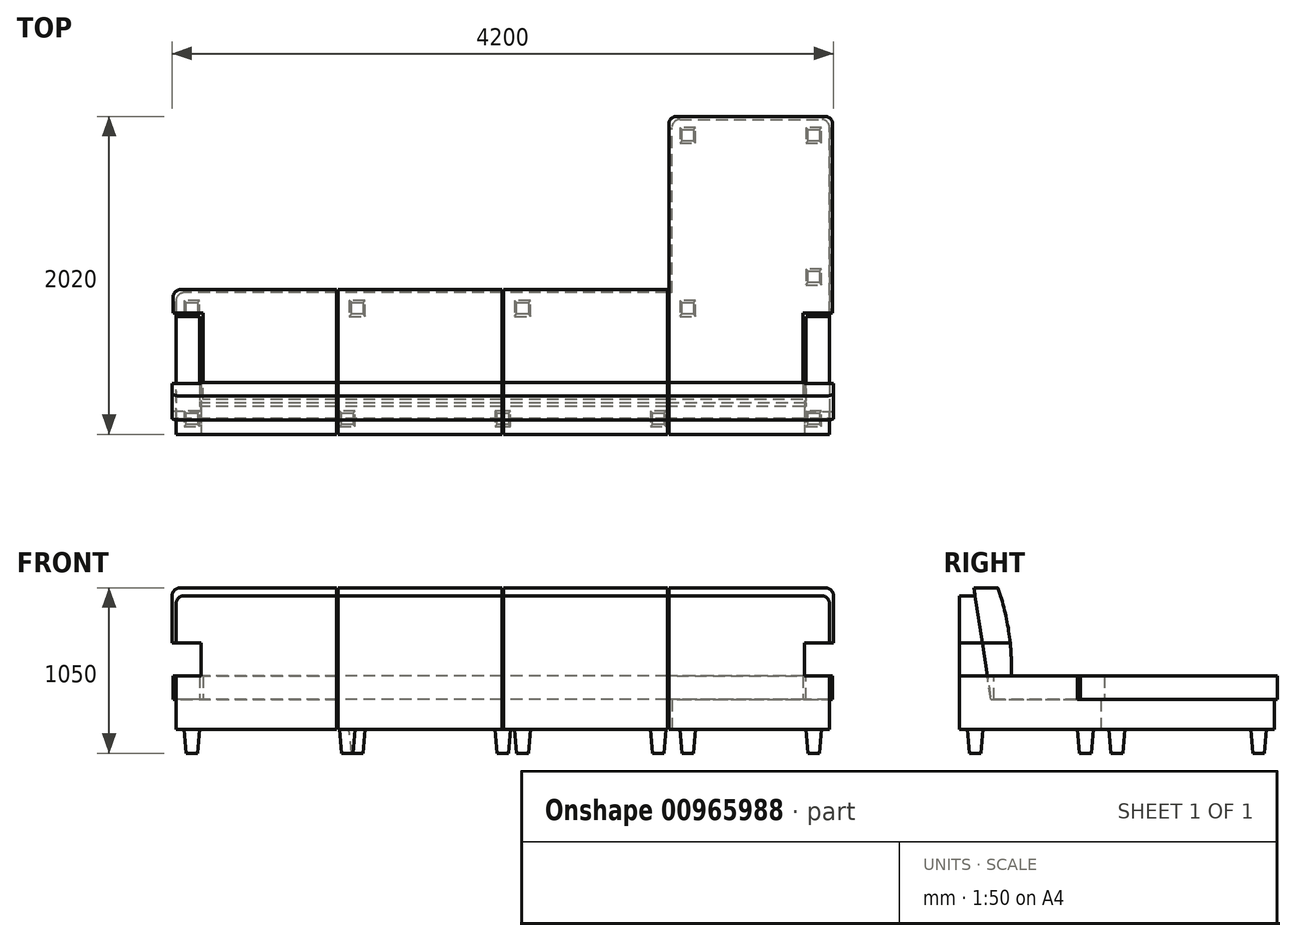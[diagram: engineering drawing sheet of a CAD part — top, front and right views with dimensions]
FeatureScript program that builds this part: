
annotation { "Feature Type Name" : "Feature", "Feature Type Description" : "" }
export const myFeature = defineFeature(function(context is Context, id is Id, definition is map)
    precondition{}
    {
        {
            var Q0;
            Q0=qCreatedBy(makeId("Right.planeOp"),FACE);
            var sketch = newSketch(context, id + "F0", { "sketchPlane" : qUnion([Q0])});
            skLineSegment(sketch, "E0", {"start": v(0, 150) * mm, "end": v(0, 1000) * mm});
            skLineSegment(sketch, "E1", {"start": v(0, 1000) * mm, "end": v(100, 1000) * mm});
            skLineSegment(sketch, "E2", {"start": v(100, 1000) * mm, "end": v(200, 340) * mm});
            skLineSegment(sketch, "E3", {"start": v(200, 340) * mm, "end": v(900, 340) * mm});
            skLineSegment(sketch, "E4", {"start": v(900, 340) * mm, "end": v(900, 150) * mm});
            skLineSegment(sketch, "E5", {"start": v(900, 150) * mm, "end": v(0, 150) * mm});
            skSolve(sketch);
        }
        {
            var Q0;
            Q0 = qSketchRegion(id + "F0", true);
            extrude(context, id + "F1", {"entities" : qUnion([Q0]), "depth" : 4150 * mm, "offsetDistance" : 25 * mm});
        }
        {
            var Q0;
            Q0=makeQuery(id+"F1.opExtrude","SWEPT_FACE",FACE,{"disambiguationData":[OSD([sQuery(id+"F0.wireOp",EDGE,"E5")])]});
            var sketch = newSketch(context, id + "F2", { "sketchPlane" : qUnion([Q0])});
            skLineSegment(sketch, "E6.bottom", {"start": v(3150, 0) * mm, "end": v(4150, 0) * mm});
            skLineSegment(sketch, "E6.top", {"start": v(3150, -2000) * mm, "end": v(4150, -2000) * mm});
            skLineSegment(sketch, "E6.left", {"start": v(3150, 0) * mm, "end": v(3150, -2000) * mm});
            skLineSegment(sketch, "E6.right", {"start": v(4150, 0) * mm, "end": v(4150, -2000) * mm});
            skSolve(sketch);
        }
        {
            var Q0;
            {var subQ0=sQuery(id+"F2.wireOp",EDGE,"E6.top");Q0=makeQuery(id+"F2.imprint","IMPRINT",FACE,{"disambiguationData":[TD([[makeQuery(id+"F2.imprint","IMPRINT",EDGE,{"derivedFrom":subQ0}),1.0]])]});}
            var Q1;
            Q1=makeQuery(id+"F1.opExtrude","SWEPT_FACE",FACE,{"disambiguationData":[OSD([sQuery(id+"F0.wireOp",EDGE,"E3")])]});
            extrude(context, id + "F3", {"entities" : qUnion([Q0]), "operationType" : NewBodyOperationType.ADD, "endBound" : BoundingType.UP_TO_SURFACE, "oppositeDirection" : true, "depth" : 25 * mm, "endBoundEntityFace" : qUnion([Q1]), "offsetDistance" : 25 * mm});
        }
        {
            var Q0;
            Q0=qCreatedBy(makeId("Front.planeOp"),FACE);
            var sketch = newSketch(context, id + "F4", { "sketchPlane" : qUnion([Q0])});
            skLineSegment(sketch, "E7.bottom", {"start": v(150, 690) * mm, "end": v(0, 690) * mm});
            skLineSegment(sketch, "E7.top", {"start": v(150, 340) * mm, "end": v(0, 340) * mm});
            skLineSegment(sketch, "E7.left", {"start": v(150, 690) * mm, "end": v(150, 340) * mm});
            skLineSegment(sketch, "E7.right", {"start": v(0, 690) * mm, "end": v(0, 340) * mm});
            skSolve(sketch);
        }
        {
            var Q0;
            Q0 = qSketchRegion(id + "F4", true);
            var Q1;
            Q1=makeQuery(id+"F1.opExtrude","SWEPT_FACE",FACE,{"disambiguationData":[OSD([sQuery(id+"F0.wireOp",EDGE,"E4")])]});
            extrude(context, id + "F5", {"entities" : qUnion([Q0]), "operationType" : NewBodyOperationType.ADD, "oppositeDirection" : true, "depth" : 750 * mm, "endBoundEntityFace" : qUnion([Q1]), "offsetDistance" : 25 * mm});
        }
        {
            var Q0;
            Q0=qCreatedBy(makeId("Front.planeOp"),FACE);
            var sketch = newSketch(context, id + "F6", { "sketchPlane" : qUnion([Q0])});
            skLineSegment(sketch, "E8.bottom", {"start": v(4150, 690) * mm, "end": v(4000, 690) * mm});
            skLineSegment(sketch, "E8.top", {"start": v(4150, 150) * mm, "end": v(4000, 150) * mm});
            skLineSegment(sketch, "E8.left", {"start": v(4150, 690) * mm, "end": v(4150, 150) * mm});
            skLineSegment(sketch, "E8.right", {"start": v(4000, 690) * mm, "end": v(4000, 150) * mm});
            skSolve(sketch);
        }
        {
            var Q0;
            Q0 = qSketchRegion(id + "F6", true);
            extrude(context, id + "F7", {"entities" : qUnion([Q0]), "operationType" : NewBodyOperationType.ADD, "oppositeDirection" : true, "depth" : 750 * mm, "offsetDistance" : 25 * mm});
        }
        {
            var Q0;
            Q0=makeQuery(id+"F3.boolean.opBoolean","MERGE",FACE,{"derivedFrom":[makeQuery(id+"F1.opExtrude","SWEPT_FACE",FACE,{"disambiguationData":[OSD([sQuery(id+"F0.wireOp",EDGE,"E3")])]}),makeQuery(id+"F3.opExtrude","CAP_FACE",FACE,{"disambiguationData":[OSD([sQuery(id+"F0.wireOp",EDGE,"E4"),sQuery(id+"F0.wireOp",EDGE,"E5"),sQuery(id+"F2.wireOp",EDGE,"E6.top"),sQuery(id+"F2.wireOp",EDGE,"E6.left"),sQuery(id+"F2.wireOp",EDGE,"E6.right")])],"isStart":false})]});
            var sketch = newSketch(context, id + "F8", { "sketchPlane" : qUnion([Q0])});
            skLineSegment(sketch, "E9", {"start": v(4170, 770) * mm, "end": v(3980, 770) * mm});
            skLineSegment(sketch, "E10", {"start": v(3980, 770) * mm, "end": v(3980, 220) * mm});
            skLineSegment(sketch, "E11", {"start": v(3980, 220) * mm, "end": v(170, 220) * mm});
            skLineSegment(sketch, "E12", {"start": v(170, 220) * mm, "end": v(170, 770) * mm});
            skLineSegment(sketch, "E13", {"start": v(170, 770) * mm, "end": v(-20, 770) * mm});
            skLineSegment(sketch, "E14", {"start": v(-20, 770) * mm, "end": v(-20, 920) * mm});
            skLineSegment(sketch, "E15", {"start": v(-20, 920) * mm, "end": v(3130, 920) * mm});
            skLineSegment(sketch, "E16", {"start": v(3130, 920) * mm, "end": v(3130, 2020) * mm});
            skLineSegment(sketch, "E17", {"start": v(3130, 2020) * mm, "end": v(4170, 2020) * mm});
            skLineSegment(sketch, "E18", {"start": v(4170, 2020) * mm, "end": v(4170, 770) * mm});
            skSolve(sketch);
        }
        {
            var Q0;
            Q0 = qSketchRegion(id + "F8", true);
            extrude(context, id + "F9", {"entities" : qUnion([Q0]), "depth" : 150 * mm, "offsetDistance" : 25 * mm});
        }
        {
            var Q0;
            Q0=qCreatedBy(makeId("Right.planeOp"),FACE);
            var sketch = newSketch(context, id + "F10", { "sketchPlane" : qUnion([Q0])});
            skLineSegment(sketch, "E19.bottom", {"start": v(92.42, 1050) * mm, "end": v(244.14, 1050) * mm});
            skLineSegment(sketch, "E19.top", {"start": v(177.27, 490) * mm, "end": v(328.98, 490) * mm});
            skLineSegment(sketch, "E19.left", {"start": v(92.42, 1050) * mm, "end": v(177.27, 490) * mm});
            skLineSegment(sketch, "E19.right", {"start": v(244.14, 1050) * mm, "end": v(328.98, 490) * mm, "construction": true});
            skArc(sketch, "E20", {"start": v(328.98, 490) * mm, "mid": v(313.23, 774.04) * mm, "end": v(244.14, 1050) * mm});
            skSolve(sketch);
        }
        {
            var Q0;
            Q0 = qSketchRegion(id + "F10", true);
            var Q1;
            Q1=makeQuery(id+"Fd29iBY72BFaIf1_4.opBoolean","MERGE",FACE,{"derivedFrom":[makeQuery(id+"F3.boolean.opBoolean","MERGE",FACE,{"derivedFrom":[makeQuery(id+"F1.opExtrude","CAP_FACE",FACE,{"disambiguationData":[OSD([sQuery(id+"F0.wireOp",EDGE,"E0"),sQuery(id+"F0.wireOp",EDGE,"E1"),sQuery(id+"F0.wireOp",EDGE,"E2"),sQuery(id+"F0.wireOp",EDGE,"E3"),sQuery(id+"F0.wireOp",EDGE,"E4"),sQuery(id+"F0.wireOp",EDGE,"E5")])],"isStart":false}),makeQuery(id+"F3.opExtrude","SWEPT_FACE",FACE,{"disambiguationData":[OSD([sQuery(id+"F2.wireOp",EDGE,"E6.right")])]})]}),makeQuery(id+"F7.opExtrude","SWEPT_FACE",FACE,{"disambiguationData":[OSD([sQuery(id+"F6.wireOp",EDGE,"E8.left")])]})]});
            extrude(context, id + "F11", {"entities" : qUnion([Q0]), "endBound" : BoundingType.UP_TO_SURFACE, "depth" : 25 * mm, "endBoundEntityFace" : qUnion([Q1]), "hasOffset" : true, "offsetDistance" : 25 * mm, "offsetOppositeDirection" : true, "hasSecondDirection" : true, "secondDirectionOppositeDirection" : true, "secondDirectionDepth" : 25 * mm});
        }
        {
            var Q0;
            Q0=qCreatedBy(makeId("Front.planeOp"),FACE);
            var sketch = newSketch(context, id + "F12", { "sketchPlane" : qUnion([Q0])});
            skLineSegment(sketch, "E21.bottom", {"start": v(4175, 700) * mm, "end": v(3990, 700) * mm});
            skLineSegment(sketch, "E21.top", {"start": v(4175, 490) * mm, "end": v(3990, 490) * mm});
            skLineSegment(sketch, "E21.left", {"start": v(4175, 700) * mm, "end": v(4175, 490) * mm});
            skLineSegment(sketch, "E21.right", {"start": v(3990, 700) * mm, "end": v(3990, 490) * mm});
            skLineSegment(sketch, "E22.bottom", {"start": v(-25, 490) * mm, "end": v(160, 490) * mm});
            skLineSegment(sketch, "E22.top", {"start": v(-25, 700) * mm, "end": v(160, 700) * mm});
            skLineSegment(sketch, "E22.left", {"start": v(-25, 490) * mm, "end": v(-25, 700) * mm});
            skLineSegment(sketch, "E22.right", {"start": v(160, 490) * mm, "end": v(160, 700) * mm});
            skSolve(sketch);
        }
        {
            var Q0;
            Q0 = qSketchRegion(id + "F12", true);
            extrude(context, id + "F13", {"entities" : qUnion([Q0]), "operationType" : NewBodyOperationType.REMOVE, "endBound" : BoundingType.THROUGH_ALL, "oppositeDirection" : true, "depth" : 25 * mm, "offsetDistance" : 25 * mm});
        }
        {
            var Q0;
            Q0=makeQuery(id+"F9.opExtrude","CAP_FACE",FACE,{"disambiguationData":[OSD([sQuery(id+"F8.wireOp",EDGE,"E9"),sQuery(id+"F8.wireOp",EDGE,"E10"),sQuery(id+"F8.wireOp",EDGE,"E11"),sQuery(id+"F8.wireOp",EDGE,"E12"),sQuery(id+"F8.wireOp",EDGE,"E13"),sQuery(id+"F8.wireOp",EDGE,"E14"),sQuery(id+"F8.wireOp",EDGE,"E15"),sQuery(id+"F8.wireOp",EDGE,"E16"),sQuery(id+"F8.wireOp",EDGE,"E17"),sQuery(id+"F8.wireOp",EDGE,"E18")])],"isStart":false});
            var sketch = newSketch(context, id + "F14", { "sketchPlane" : qUnion([Q0])});
            skLineSegment(sketch, "E23.bottom", {"start": v(3130, 920) * mm, "end": v(3120, 920) * mm});
            skLineSegment(sketch, "E23.top", {"start": v(3130, 0) * mm, "end": v(3120, 0) * mm});
            skLineSegment(sketch, "E23.left", {"start": v(3130, 920) * mm, "end": v(3130, 0) * mm});
            skLineSegment(sketch, "E23.right", {"start": v(3120, 920) * mm, "end": v(3120, 0) * mm});
            skLineSegment(sketch, "E24.bottom", {"start": v(2080, 920) * mm, "end": v(2070, 920) * mm});
            skLineSegment(sketch, "E24.top", {"start": v(2080, 0) * mm, "end": v(2070, 0) * mm});
            skLineSegment(sketch, "E24.left", {"start": v(2070, 920) * mm, "end": v(2070, 0) * mm});
            skLineSegment(sketch, "E24.right", {"start": v(2080, 920) * mm, "end": v(2080, 0) * mm});
            skLineSegment(sketch, "E25.bottom", {"start": v(1030, 920) * mm, "end": v(1020, 920) * mm});
            skLineSegment(sketch, "E25.top", {"start": v(1030, 0) * mm, "end": v(1020, 0) * mm});
            skLineSegment(sketch, "E25.left", {"start": v(1030, 920) * mm, "end": v(1030, 0) * mm});
            skLineSegment(sketch, "E25.right", {"start": v(1020, 920) * mm, "end": v(1020, 0) * mm});
            skLineSegment(sketch, "E26", {"start": v(1025, 920) * mm, "end": v(1025, 0) * mm, "construction": true});
            skLineSegment(sketch, "E27", {"start": v(3125, 920) * mm, "end": v(3125, 0) * mm, "construction": true});
            skLineSegment(sketch, "E28", {"start": v(2075, 920) * mm, "end": v(2075, 0) * mm, "construction": true});
            skLineSegment(sketch, "E29", {"start": v(1025, 460) * mm, "end": v(3125, 460) * mm, "construction": true});
            skPoint(sketch, "E30", {"position": v(2075, 460) * mm});
            skLineSegment(sketch, "E31", {"start": v(3130, 460) * mm, "end": v(3980, 460) * mm, "construction": true});
            skLineSegment(sketch, "E32", {"start": v(1020, 460) * mm, "end": v(170, 460) * mm, "construction": true});
            skSolve(sketch);
        }
        {
            var Q0;
            Q0 = qSketchRegion(id + "F14", true);
            extrude(context, id + "F15", {"entities" : qUnion([Q0]), "operationType" : NewBodyOperationType.REMOVE, "endBound" : BoundingType.THROUGH_ALL, "depth" : 25 * mm, "offsetDistance" : 25 * mm, "hasSecondDirection" : true, "secondDirectionBound" : SecondDirectionBoundingType.THROUGH_ALL, "secondDirectionOppositeDirection" : true, "secondDirectionDepth" : 25 * mm});
        }
        {
            var Q0;
            Q0=makeQuery(id+"F11.opExtrude","CAP_EDGE",EDGE,{"disambiguationData":[OSD([sQuery(id+"F10.wireOp",EDGE,"E19.bottom")])],"isStart":false});
            var Q1;
            Q1=makeQuery(id+"F1.opExtrude","CAP_EDGE",EDGE,{"disambiguationData":[OSD([sQuery(id+"F0.wireOp",EDGE,"E1")])],"isStart":false});
            var Q2;
            Q2=makeQuery(id+"F7.opExtrude","CAP_EDGE",EDGE,{"disambiguationData":[OSD([sQuery(id+"F6.wireOp",EDGE,"E8.bottom")])],"isStart":false});
            var Q3;
            Q3=makeQuery(id+"F3.opExtrude","SWEPT_EDGE",EDGE,{"disambiguationData":[OSD([sQuery(id+"F2.wireOp",EDGE,"E6.top"),sQuery(id+"F2.wireOp",EDGE,"E6.right")])]});
            var Q4;
            Q4=makeQuery(id+"F3.opExtrude","SWEPT_EDGE",EDGE,{"disambiguationData":[OSD([sQuery(id+"F2.wireOp",EDGE,"E6.top"),sQuery(id+"F2.wireOp",EDGE,"E6.left")])]});
            var Q5;
            Q5=makeQuery(id+"F9.opExtrude","SWEPT_EDGE",EDGE,{"disambiguationData":[OSD([sQuery(id+"F8.wireOp",EDGE,"E16"),sQuery(id+"F8.wireOp",EDGE,"E17")])]});
            var Q6;
            Q6=makeQuery(id+"F9.opExtrude","SWEPT_EDGE",EDGE,{"disambiguationData":[OSD([sQuery(id+"F8.wireOp",EDGE,"E17"),sQuery(id+"F8.wireOp",EDGE,"E18")])]});
            var Q7;
            Q7=makeQuery(id+"F9.opExtrude","SWEPT_EDGE",EDGE,{"disambiguationData":[OSD([sQuery(id+"F8.wireOp",EDGE,"E14"),sQuery(id+"F8.wireOp",EDGE,"E15")])]});
            var Q8;
            Q8=makeQuery(id+"F1.opExtrude","CAP_EDGE",EDGE,{"disambiguationData":[OSD([sQuery(id+"F0.wireOp",EDGE,"E4")])],"isStart":true});
            var Q9;
            Q9=makeQuery(id+"F5.opExtrude","CAP_EDGE",EDGE,{"disambiguationData":[OSD([sQuery(id+"F4.wireOp",EDGE,"E7.bottom")])],"isStart":false});
            var Q10;
            Q10=makeQuery(id+"F11.opExtrude","CAP_EDGE",EDGE,{"disambiguationData":[OSD([sQuery(id+"F10.wireOp",EDGE,"E19.bottom")])],"isStart":true});
            var Q11;
            Q11=makeQuery(id+"F1.opExtrude","CAP_EDGE",EDGE,{"disambiguationData":[OSD([sQuery(id+"F0.wireOp",EDGE,"E1")])],"isStart":true});
            fillet(context, id + "F16", {"entities" : qUnion([Q0, Q1, Q2, Q3, Q4, Q5, Q6, Q7, Q8, Q9, Q10, Q11]), "radius" : 50 * mm, "tangentPropagation" : true, "allowEdgeOverflow" : false});
        }
        {
            var Q0;
            {var subQ0=sQuery(id+"F0.wireOp",EDGE,"E5");Q0=makeQuery(id+"F3.boolean.opBoolean","MERGE",FACE,{"derivedFrom":[makeQuery(id+"F1.opExtrude","SWEPT_FACE",FACE,{"disambiguationData":[OSD([subQ0])]}),makeQuery(id+"F3.opExtrude","CAP_FACE",FACE,{"disambiguationData":[OSD([sQuery(id+"F0.wireOp",EDGE,"E4"),subQ0,sQuery(id+"F2.wireOp",EDGE,"E6.top"),sQuery(id+"F2.wireOp",EDGE,"E6.left"),sQuery(id+"F2.wireOp",EDGE,"E6.right")])],"isStart":true})]});}
            var sketch = newSketch(context, id + "F17", { "sketchPlane" : qUnion([Q0])});
            skLineSegment(sketch, "E33.bottom", {"start": v(150, -150) * mm, "end": v(50, -150) * mm});
            skLineSegment(sketch, "E33.top", {"start": v(150, -50) * mm, "end": v(50, -50) * mm});
            skLineSegment(sketch, "E33.left", {"start": v(150, -150) * mm, "end": v(150, -50) * mm});
            skLineSegment(sketch, "E33.right", {"start": v(50, -150) * mm, "end": v(50, -50) * mm});
            skLineSegment(sketch, "E34", {"start": v(150, -150) * mm, "end": v(50, -50) * mm, "construction": true});
            skPoint(sketch, "E35", {"position": v(100, -100) * mm});
            skLineSegment(sketch, "E36.bottom", {"start": v(1037.5, -50) * mm, "end": v(1137.5, -50) * mm});
            skLineSegment(sketch, "E36.top", {"start": v(1037.5, -150) * mm, "end": v(1137.5, -150) * mm});
            skLineSegment(sketch, "E36.left", {"start": v(1037.5, -50) * mm, "end": v(1037.5, -150) * mm});
            skLineSegment(sketch, "E36.right", {"start": v(1137.5, -50) * mm, "end": v(1137.5, -150) * mm});
            skLineSegment(sketch, "E37.bottom", {"start": v(2025, -50) * mm, "end": v(2125, -50) * mm});
            skLineSegment(sketch, "E37.top", {"start": v(2025, -150) * mm, "end": v(2125, -150) * mm});
            skLineSegment(sketch, "E37.left", {"start": v(2025, -50) * mm, "end": v(2025, -150) * mm});
            skLineSegment(sketch, "E37.right", {"start": v(2125, -50) * mm, "end": v(2125, -150) * mm});
            skLineSegment(sketch, "E38.bottom", {"start": v(50, -750) * mm, "end": v(150, -750) * mm});
            skLineSegment(sketch, "E38.top", {"start": v(50, -850) * mm, "end": v(150, -850) * mm});
            skLineSegment(sketch, "E38.left", {"start": v(50, -750) * mm, "end": v(50, -850) * mm});
            skLineSegment(sketch, "E38.right", {"start": v(150, -750) * mm, "end": v(150, -850) * mm});
            skLineSegment(sketch, "E39.bottom", {"start": v(1100, -750) * mm, "end": v(1200, -750) * mm});
            skLineSegment(sketch, "E39.top", {"start": v(1100, -850) * mm, "end": v(1200, -850) * mm});
            skLineSegment(sketch, "E39.left", {"start": v(1100, -750) * mm, "end": v(1100, -850) * mm});
            skLineSegment(sketch, "E39.right", {"start": v(1200, -750) * mm, "end": v(1200, -850) * mm});
            skLineSegment(sketch, "E40.bottom", {"start": v(2150, -750) * mm, "end": v(2250, -750) * mm});
            skLineSegment(sketch, "E40.top", {"start": v(2150, -850) * mm, "end": v(2250, -850) * mm});
            skLineSegment(sketch, "E40.left", {"start": v(2150, -750) * mm, "end": v(2150, -850) * mm});
            skLineSegment(sketch, "E40.right", {"start": v(2250, -750) * mm, "end": v(2250, -850) * mm});
            skLineSegment(sketch, "E41.bottom", {"start": v(3200, -1850) * mm, "end": v(3300, -1850) * mm});
            skLineSegment(sketch, "E41.top", {"start": v(3200, -1950) * mm, "end": v(3300, -1950) * mm});
            skLineSegment(sketch, "E41.left", {"start": v(3200, -1850) * mm, "end": v(3200, -1950) * mm});
            skLineSegment(sketch, "E41.right", {"start": v(3300, -1850) * mm, "end": v(3300, -1950) * mm});
            skLineSegment(sketch, "E42.bottom", {"start": v(4000, -50) * mm, "end": v(4100, -50) * mm});
            skLineSegment(sketch, "E42.top", {"start": v(4000, -150) * mm, "end": v(4100, -150) * mm});
            skLineSegment(sketch, "E42.left", {"start": v(4000, -50) * mm, "end": v(4000, -150) * mm});
            skLineSegment(sketch, "E42.right", {"start": v(4100, -50) * mm, "end": v(4100, -150) * mm});
            skLineSegment(sketch, "E43", {"start": v(1037.5, -50) * mm, "end": v(1137.5, -150) * mm, "construction": true});
            skLineSegment(sketch, "E44", {"start": v(50, -750) * mm, "end": v(150, -850) * mm, "construction": true});
            skLineSegment(sketch, "E45", {"start": v(1100, -750) * mm, "end": v(1200, -850) * mm, "construction": true});
            skLineSegment(sketch, "E46", {"start": v(2025, -50) * mm, "end": v(2125, -150) * mm, "construction": true});
            skLineSegment(sketch, "E47", {"start": v(2150, -750) * mm, "end": v(2250, -850) * mm, "construction": true});
            skLineSegment(sketch, "E48", {"start": v(4000, -50) * mm, "end": v(4100, -150) * mm, "construction": true});
            skLineSegment(sketch, "E49", {"start": v(3200, -1850) * mm, "end": v(3300, -1950) * mm, "construction": true});
            skLineSegment(sketch, "E50.bottom", {"start": v(4000, -1850) * mm, "end": v(4100, -1850) * mm});
            skLineSegment(sketch, "E50.top", {"start": v(4000, -1950) * mm, "end": v(4100, -1950) * mm});
            skLineSegment(sketch, "E50.left", {"start": v(4000, -1850) * mm, "end": v(4000, -1950) * mm});
            skLineSegment(sketch, "E50.right", {"start": v(4100, -1850) * mm, "end": v(4100, -1950) * mm});
            skLineSegment(sketch, "E51.bottom", {"start": v(4000, -950) * mm, "end": v(4100, -950) * mm});
            skLineSegment(sketch, "E51.top", {"start": v(4000, -1050) * mm, "end": v(4100, -1050) * mm});
            skLineSegment(sketch, "E51.left", {"start": v(4000, -950) * mm, "end": v(4000, -1050) * mm});
            skLineSegment(sketch, "E51.right", {"start": v(4100, -950) * mm, "end": v(4100, -1050) * mm});
            skLineSegment(sketch, "E52.bottom", {"start": v(3200, -750) * mm, "end": v(3300, -750) * mm});
            skLineSegment(sketch, "E52.top", {"start": v(3200, -850) * mm, "end": v(3300, -850) * mm});
            skLineSegment(sketch, "E52.left", {"start": v(3200, -750) * mm, "end": v(3200, -850) * mm});
            skLineSegment(sketch, "E52.right", {"start": v(3300, -750) * mm, "end": v(3300, -850) * mm});
            skLineSegment(sketch, "E53.bottom", {"start": v(3012.5, -50) * mm, "end": v(3112.5, -50) * mm});
            skLineSegment(sketch, "E53.top", {"start": v(3012.5, -150) * mm, "end": v(3112.5, -150) * mm});
            skLineSegment(sketch, "E53.left", {"start": v(3012.5, -50) * mm, "end": v(3012.5, -150) * mm});
            skLineSegment(sketch, "E53.right", {"start": v(3112.5, -50) * mm, "end": v(3112.5, -150) * mm});
            skLineSegment(sketch, "E54", {"start": v(3012.5, -50) * mm, "end": v(3112.5, -150) * mm, "construction": true});
            skLineSegment(sketch, "E55", {"start": v(3200, -750) * mm, "end": v(3300, -850) * mm, "construction": true});
            skLineSegment(sketch, "E56", {"start": v(4000, -950) * mm, "end": v(4100, -1050) * mm, "construction": true});
            skLineSegment(sketch, "E57", {"start": v(4000, -1850) * mm, "end": v(4100, -1950) * mm, "construction": true});
            skPoint(sketch, "E58", {"position": v(1087.5, -100) * mm});
            skPoint(sketch, "E59", {"position": v(2075, -100) * mm});
            skPoint(sketch, "E60", {"position": v(1150, -800) * mm});
            skPoint(sketch, "E61", {"position": v(100, -800) * mm});
            skPoint(sketch, "E62", {"position": v(2200, -800) * mm});
            skPoint(sketch, "E63", {"position": v(3062.5, -100) * mm});
            skPoint(sketch, "E64", {"position": v(3250, -800) * mm});
            skPoint(sketch, "E65", {"position": v(4050, -100) * mm});
            skPoint(sketch, "E66", {"position": v(4050, -1000) * mm});
            skPoint(sketch, "E67", {"position": v(4050, -1900) * mm});
            skPoint(sketch, "E68", {"position": v(3250, -1900) * mm});
            skLineSegment(sketch, "E69", {"start": v(3250, -1900) * mm, "end": v(4050, -1900) * mm});
            skLineSegment(sketch, "E70", {"start": v(3250, -1900) * mm, "end": v(3250, -800) * mm, "construction": true});
            skLineSegment(sketch, "E71", {"start": v(100, -100) * mm, "end": v(100, -800) * mm, "construction": true});
            skLineSegment(sketch, "E72", {"start": v(3250, -800) * mm, "end": v(2200, -800) * mm, "construction": true});
            skLineSegment(sketch, "E73", {"start": v(1150, -800) * mm, "end": v(2200, -800) * mm, "construction": true});
            skLineSegment(sketch, "E74", {"start": v(100, -800) * mm, "end": v(1150, -800) * mm, "construction": true});
            skLineSegment(sketch, "E75", {"start": v(4050, -100) * mm, "end": v(4050, -1000) * mm, "construction": true});
            skLineSegment(sketch, "E76", {"start": v(4050, -1900) * mm, "end": v(4050, -1000) * mm, "construction": true});
            skLineSegment(sketch, "E77", {"start": v(4050, -100) * mm, "end": v(3062.5, -100) * mm, "construction": true});
            skLineSegment(sketch, "E78", {"start": v(3062.5, -100) * mm, "end": v(2075, -100) * mm, "construction": true});
            skLineSegment(sketch, "E79", {"start": v(2075, -100) * mm, "end": v(1087.5, -100) * mm, "construction": true});
            skLineSegment(sketch, "E80", {"start": v(100, -100) * mm, "end": v(1087.5, -100) * mm, "construction": true});
            skSolve(sketch);
        }
        {
            var Q0;
            Q0 = qSketchRegion(id + "F17", true);
            var Q1;
            Q1=qCreatedBy(makeId("Top.planeOp"),FACE);
            extrude(context, id + "F18", {"entities" : qUnion([Q0]), "endBound" : BoundingType.UP_TO_SURFACE, "depth" : 25 * mm, "endBoundEntityFace" : qUnion([Q1]), "offsetDistance" : 25 * mm, "hasDraft" : true, "draftAngle" : 5 * degree, "draftPullDirection" : true});
        }
    });
